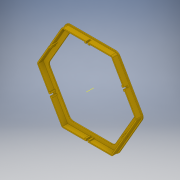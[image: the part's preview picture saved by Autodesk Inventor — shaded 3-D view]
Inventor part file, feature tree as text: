
AUTODESK INVENTOR PART (.ipt)
format: ipt  version: 2019 (Build 230136000, 136)  size: 269,824 bytes
history: native  units: mm
features: extrude x5, sketch x5, projected_geometry x3, fillet x2, other x1, pattern_circular x1
ambient origin geometry x8: Origin, YZ Plane, XZ Plane, XY Plane, X Axis, Y Axis, Z Axis, Center Point
bodies: Solid1 (feature_tree)
feature tree (17):
  extrude  "Extrusion1"  Depth=2.0mm
  extrude  "Extrusion5"  Depth=2.0mm
  extrude  "Extrusion6"  Depth=10.0mm
  fillet  "Fillet1"  [1 undecoded]
  fillet  "Fillet2"  Radius=8.0mm
  extrude  "Extrusion7"  TaperAngle=0.0deg  [1 undecoded]
  extrude  "Extrusion8"  Depth=4.0mm
  other  "Work Axis2"
  pattern_circular  "Circular Pattern1"  [2 undecoded]
  sketch  "Sketch1"  dims[d0=175.0mm d1=2.0mm]
  sketch  "Sketch5"  dims[d2=0.0mm d15=2.0mm]
  projected_geometry  "Projected Loop4"
  sketch  "Sketch7"  dims[d16=2.0mm d17=10.0mm d18=0.0mm d19=8.0mm]
  projected_geometry  "Projected Loop6"
  sketch  "Sketch8"  dims[d20=7.0mm d21=0.0mm]
  sketch  "Sketch9"  dims[d22=10.0mm d23=4.0mm d24=10.0mm d25=3.3mm d26=7.0mm d27=0.0mm d28=4.0mm d29=3.0mm d30=5.0mm d31=0.0mm d32=60.0mm d33=360.0deg]
  projected_geometry  "Projected Loop7"
note: 4 required parameter values undecoded (feature->parameter linkage not recoverable at this tier; creation-order binding heuristic only, values carry confidence <= 0.55)
